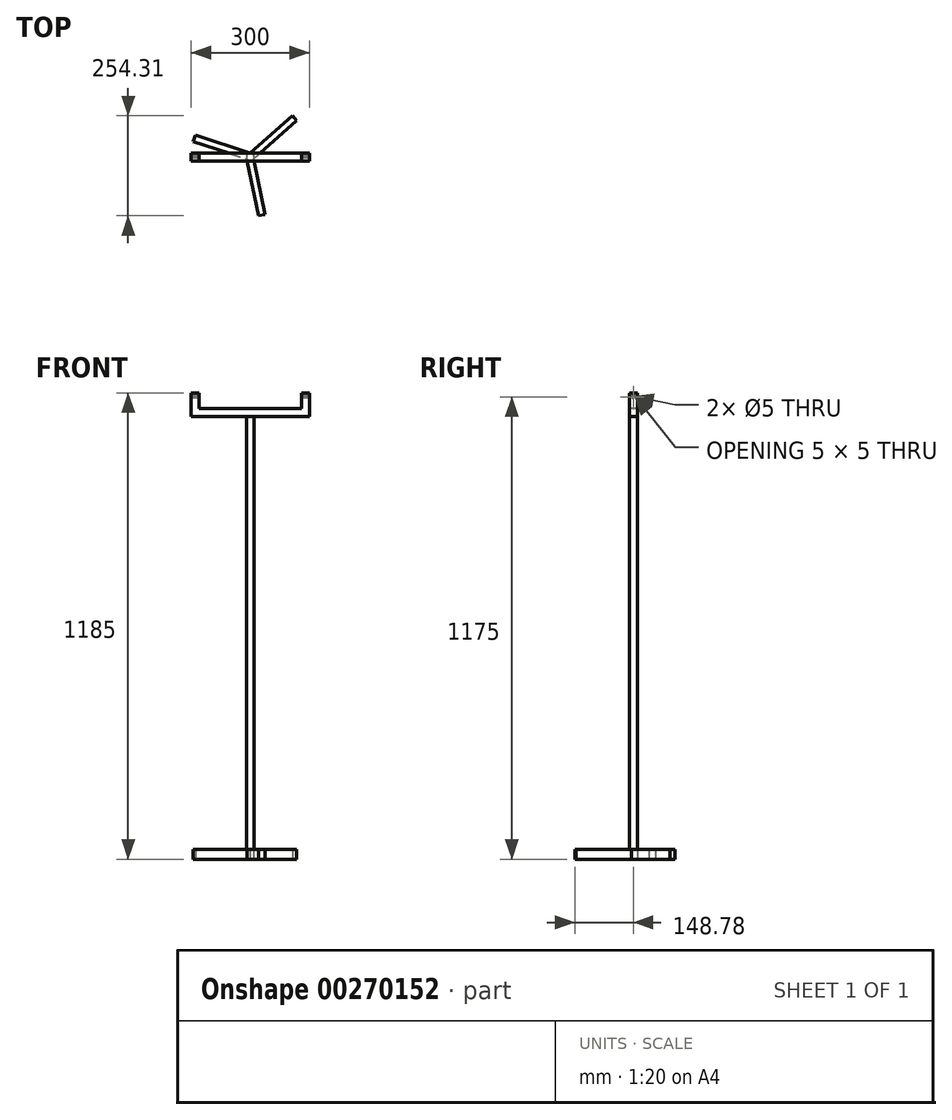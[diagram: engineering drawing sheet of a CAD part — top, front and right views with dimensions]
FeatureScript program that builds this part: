
annotation { "Feature Type Name" : "Feature", "Feature Type Description" : "" }
export const myFeature = defineFeature(function(context is Context, id is Id, definition is map)
    precondition{}
    {
        {
            var Q0;
            Q0=qCreatedBy(makeId("Top.planeOp"),FACE);
            var sketch = newSketch(context, id + "F0", { "sketchPlane" : qUnion([Q0])});
            skArc(sketch, "E0", {"start": v(0, 10) * mm, "mid": v(-0.03, 10) * mm, "end": v(-0.07, 10) * mm});
            skLineSegment(sketch, "E1", {"start": v(0, 10) * mm, "end": v(-139.5, 55.93) * mm});
            skLineSegment(sketch, "E2", {"start": v(-139.5, 55.93) * mm, "end": v(-144.82, 39.79) * mm});
            skLineSegment(sketch, "E3", {"start": v(-144.82, 39.79) * mm, "end": v(-8.63, -5.06) * mm});
            skLineSegment(sketch, "E4.1.0", {"start": v(21.31, -148.78) * mm, "end": v(37.95, -145.31) * mm});
            skLineSegment(sketch, "E4.1.1", {"start": v(-8.66, -5) * mm, "end": v(21.31, -148.78) * mm});
            skLineSegment(sketch, "E4.1.2", {"start": v(37.95, -145.31) * mm, "end": v(8.7, -4.94) * mm});
            skLineSegment(sketch, "E4.2.0", {"start": v(118.2, 92.85) * mm, "end": v(106.87, 105.53) * mm});
            skLineSegment(sketch, "E4.2.1", {"start": v(8.66, -5) * mm, "end": v(118.2, 92.85) * mm});
            skLineSegment(sketch, "E4.2.2", {"start": v(106.87, 105.53) * mm, "end": v(-0.07, 10) * mm});
            skArc(sketch, "E5.trimOffspring", {"start": v(-8.66, -5) * mm, "mid": v(-8.64, -5.03) * mm, "end": v(-8.63, -5.06) * mm});
            skArc(sketch, "E6.trimOffspring", {"start": v(8.66, -5) * mm, "mid": v(8.68, -4.97) * mm, "end": v(8.7, -4.94) * mm});
            skSolve(sketch);
        }
        {
            var Q0;
            Q0=qSketchRegion(id+"F0",true);
            extrude(context, id + "F1", {"entities" : qUnion([Q0]), "depth" : 25 * mm});
        }
        {
            var Q0;
            Q0=makeQuery(id+"F1.opExtrude","CAP_FACE",FACE,{"disambiguationData":[OSD([sQuery(id+"F0.wireOp",EDGE,"E0"),sQuery(id+"F0.wireOp",EDGE,"E1"),sQuery(id+"F0.wireOp",EDGE,"E2"),sQuery(id+"F0.wireOp",EDGE,"E3"),sQuery(id+"F0.wireOp",EDGE,"E4.1.0"),sQuery(id+"F0.wireOp",EDGE,"E4.1.1"),sQuery(id+"F0.wireOp",EDGE,"E4.1.2"),sQuery(id+"F0.wireOp",EDGE,"E4.2.0"),sQuery(id+"F0.wireOp",EDGE,"E4.2.1"),sQuery(id+"F0.wireOp",EDGE,"E4.2.2")])],"isStart":false});
            var sketch = newSketch(context, id + "F2", { "sketchPlane" : qUnion([Q0])});
            skCircle(sketch, "E7", {"center": v(0, 0) * mm, "radius": 10 * mm});
            skSolve(sketch);
        }
        {
            var Q0;
            Q0=qSketchRegion(id+"F2",true);
            extrude(context, id + "F3", {"entities" : qUnion([Q0]), "depth" : 1100 * mm});
        }
        {
            var Q0;
            Q0=makeQuery(id+"F3.opExtrude","CAP_FACE",FACE,{"disambiguationData":[OSD([sQuery(id+"F2.wireOp",EDGE,"E7")])],"isStart":false});
            var sketch = newSketch(context, id + "F4", { "sketchPlane" : qUnion([Q0])});
            skLineSegment(sketch, "E8.bottom", {"start": v(150, -10) * mm, "end": v(-150, -10) * mm});
            skLineSegment(sketch, "E8.top", {"start": v(150, 10) * mm, "end": v(-150, 10) * mm});
            skLineSegment(sketch, "E8.left", {"start": v(150, -10) * mm, "end": v(150, 10) * mm});
            skLineSegment(sketch, "E8.right", {"start": v(-150, -10) * mm, "end": v(-150, 10) * mm});
            skPoint(sketch, "E8.middle", {"position": v(0, 0) * mm});
            skSolve(sketch);
        }
        {
            var Q0;
            Q0=qSketchRegion(id+"F4",true);
            extrude(context, id + "F5", {"entities" : qUnion([Q0]), "operationType" : NewBodyOperationType.ADD, "depth" : 20 * mm});
        }
        {
            var Q0;
            Q0=makeQuery(id+"F5.opExtrude","CAP_FACE",FACE,{"disambiguationData":[OSD([sQuery(id+"F4.wireOp",EDGE,"E8.bottom"),sQuery(id+"F4.wireOp",EDGE,"E8.top"),sQuery(id+"F4.wireOp",EDGE,"E8.left"),sQuery(id+"F4.wireOp",EDGE,"E8.right")])],"isStart":false});
            var sketch = newSketch(context, id + "F6", { "sketchPlane" : qUnion([Q0])});
            skLineSegment(sketch, "E9.bottom", {"start": v(-150, 10) * mm, "end": v(-130, 10) * mm});
            skLineSegment(sketch, "E9.top", {"start": v(-150, -10) * mm, "end": v(-130, -10) * mm});
            skLineSegment(sketch, "E9.left", {"start": v(-150, 10) * mm, "end": v(-150, -10) * mm});
            skLineSegment(sketch, "E9.right", {"start": v(-130, 10) * mm, "end": v(-130, -10) * mm});
            skLineSegment(sketch, "E10.bottom", {"start": v(150, 10) * mm, "end": v(130, 10) * mm});
            skLineSegment(sketch, "E10.top", {"start": v(150, -10) * mm, "end": v(130, -10) * mm});
            skLineSegment(sketch, "E10.left", {"start": v(150, 10) * mm, "end": v(150, -10) * mm});
            skLineSegment(sketch, "E10.right", {"start": v(130, 10) * mm, "end": v(130, -10) * mm});
            skSolve(sketch);
        }
        {
            var Q0;
            Q0=qSketchRegion(id+"F6",true);
            extrude(context, id + "F7", {"entities" : qUnion([Q0]), "operationType" : NewBodyOperationType.ADD, "depth" : 40 * mm});
        }
        {
            var Q0;
            Q0=makeQuery(id+"F7.boolean.opBoolean","MERGE",FACE,{"derivedFrom":[makeQuery(id+"F5.opExtrude","SWEPT_FACE",FACE,{"disambiguationData":[OSD([sQuery(id+"F4.wireOp",EDGE,"E8.right")])]}),makeQuery(id+"F7.opExtrude","SWEPT_FACE",FACE,{"disambiguationData":[OSD([sQuery(id+"F6.wireOp",EDGE,"E9.left")])]})]});
            var sketch = newSketch(context, id + "F8", { "sketchPlane" : qUnion([Q0])});
            skCircle(sketch, "E11", {"center": v(0, 1175) * mm, "radius": 2.5 * mm});
            skSolve(sketch);
        }
        {
            var Q0;
            Q0=qSketchRegion(id+"F8",true);
            extrude(context, id + "F9", {"entities" : qUnion([Q0]), "operationType" : NewBodyOperationType.REMOVE, "oppositeDirection" : true, "depth" : 500 * mm});
        }
    });
